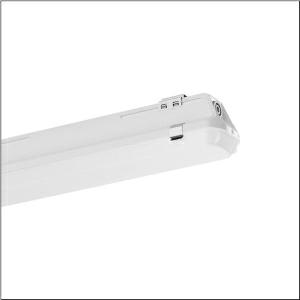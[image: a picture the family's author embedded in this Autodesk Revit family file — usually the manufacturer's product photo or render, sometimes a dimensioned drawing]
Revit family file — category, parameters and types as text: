
# Revit family: monsun_r__11_51fp22mp4b0q_0e64
name_source: partatom
category: Lighting Fixtures
units: mm (PartAtom-declared; Revit-internal decimal feet)

## family parameters
Cut with Voids When Loaded = No
Host = Face
Light Source = No
Part Type = Normal
Room Calculation Point = No
Round Connector Dimension = Use Diameter
Shared = No

## types (1)
- --- (1 x LED, 10520 lm, 66.2 W, 4000K)
    Apparent Load = 66 VA
    CIE Flux Codes = 49 78 94 96 100
    Color Rendering = 80
    Color Temperature = 4000K
    Default Elevation = 1800 mm
    Description = Monsun® 11, damp-proof luminaire, chain hanger, primary light control with lens, primary optical cover: enclosure, of PC, light emission: direct distribution, primary light characteristic: symmetric, installation type: suspended mounting, surface-mounted, horizontal mounting, vertical mounting, LED, rated luminous flux: 10.520lm, luminous efficacy: 159lm/W, light colour: 840, colour temperature: 4000K, control gear: ECG, with terminal, 3-pole, max. 2.5mm², mains connection: 220..240V, AC, 50/60Hz, rated input power: 66W, luminaire housing, of glass-fibre reinforced polyester, uncoated, bright grey, incl. chain hanger, length: 1.590mm, width: 90mm, height: 88mm, clip for enclosure, of stainless steel (V2A), ceiling mounting element, of stainless steel (V2A), chain hanger, of stainless steel (V2A), protection rating (complete): IP66, insulation class (complete): insulation class I (protective earthing), certification: CE, ENEC, VDE, UKCA, protection symbol: D, impact resistance: IK08, permissible operating ambient temperature: -35..+35°C, standard: EN 50419, EN 60598-2-1, no direct snow, no direct sun, no direct rain, for indoor or canopied outdoor use, corresponds to IFS (International Featured Standards) requirements for safety and quality in the food industry, contact your sales advisor before using the luminaires in applications with unclear chemical exposure, large temperature fluctuations or condensation-forming humidity, LABS conformity tested according to VDMA 24364:2018-05, packaging unit: 1 piece
    Height = 89 mm
    Lamp = 1 x LED
    Lamp Light Flux = 10520 lm
    Lamp Power = 66.2 W
    Lamp count = 1
    Length = 1590 mm
    Luminous efficacy = 159 lm/W
    Manufacturer = Siteco
    ModVariant = No
    Model = 51FP22MP4B0Q
    Mounting Place = Ceiling
    Mounting Type = Surface mounted
    Number of Poles = 1
    OnlyDefault = Yes
    Power Factor = 1
    Product Name = Monsun® 11
    Product group = damp-proof luminaire
    ProductGroupID = 300
    Protection Class = Protection class I
    Protection Degree = IP 66
    RLX_Detail_Level = 1
    RLX_Emergency_Light_Flux = 0 lm
    RLX_Emergency_Type = 0
    RLX_Emergency_Type_DB = No
    RlxData = <blob elided: 89981 chars, md5=edf3cba8>
    Socket = socket
    Standby Power = 0 W
    System Light Flux = 10520 lm
    System Power = 66 W
    Type Comments = factory setting: luminous flux: 100 % | (A | C | E) | 155 mA
    Type Image = l_1319650.jpg
    URL = http://relux.com
    VarID = @adj_174205
    Voltage = 0 V
    Weight = 0.00 kg
    Width = 90 mm

## geometry (parser evidence)
native form markers: Blend x4, Sweep x13
no freeform markers — native parametric forms only
